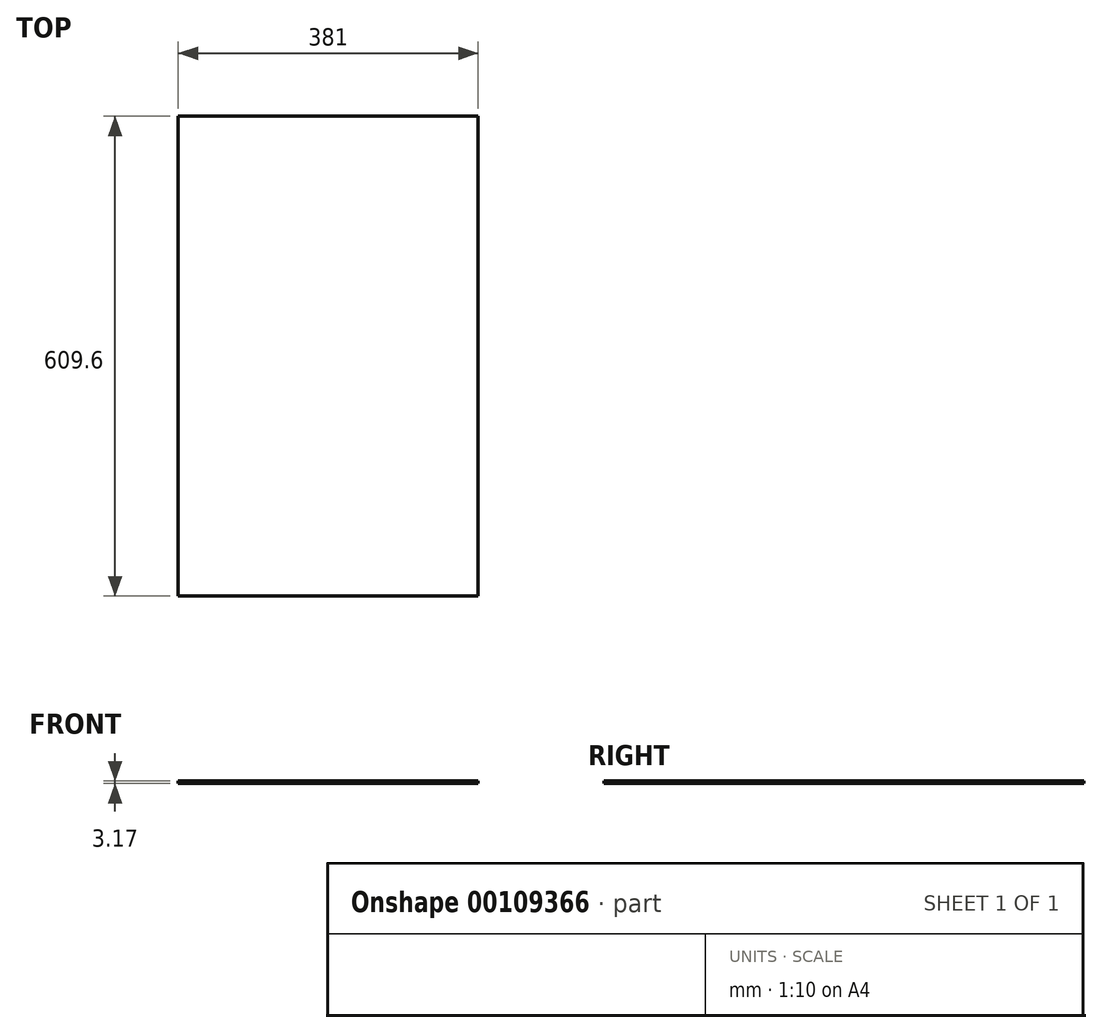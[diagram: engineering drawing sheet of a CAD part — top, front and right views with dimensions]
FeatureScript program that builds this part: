
annotation { "Feature Type Name" : "Feature", "Feature Type Description" : "" }
export const myFeature = defineFeature(function(context is Context, id is Id, definition is map)
    precondition{}
    {
        {
            var Q0;
            Q0=qCreatedBy(makeId("Top.planeOp"),FACE);
            var sketch = newSketch(context, id + "F0", { "sketchPlane" : qUnion([Q0])});
            skLineSegment(sketch, "E0.bottom", {"start": v(-190.5, 304.8) * mm, "end": v(190.5, 304.8) * mm});
            skLineSegment(sketch, "E0.top", {"start": v(-190.5, -304.8) * mm, "end": v(190.5, -304.8) * mm});
            skLineSegment(sketch, "E0.left", {"start": v(-190.5, 304.8) * mm, "end": v(-190.5, -304.8) * mm});
            skLineSegment(sketch, "E0.right", {"start": v(190.5, 304.8) * mm, "end": v(190.5, -304.8) * mm});
            skPoint(sketch, "E0.middle", {"position": v(0, 0) * mm});
            skSolve(sketch);
        }
        {
            var Q0;
            Q0 = qSketchRegion(id + "F0", true);
            extrude(context, id + "F1", {"entities" : qUnion([Q0]), "depth" : 3.17 * mm});
        }
    });
